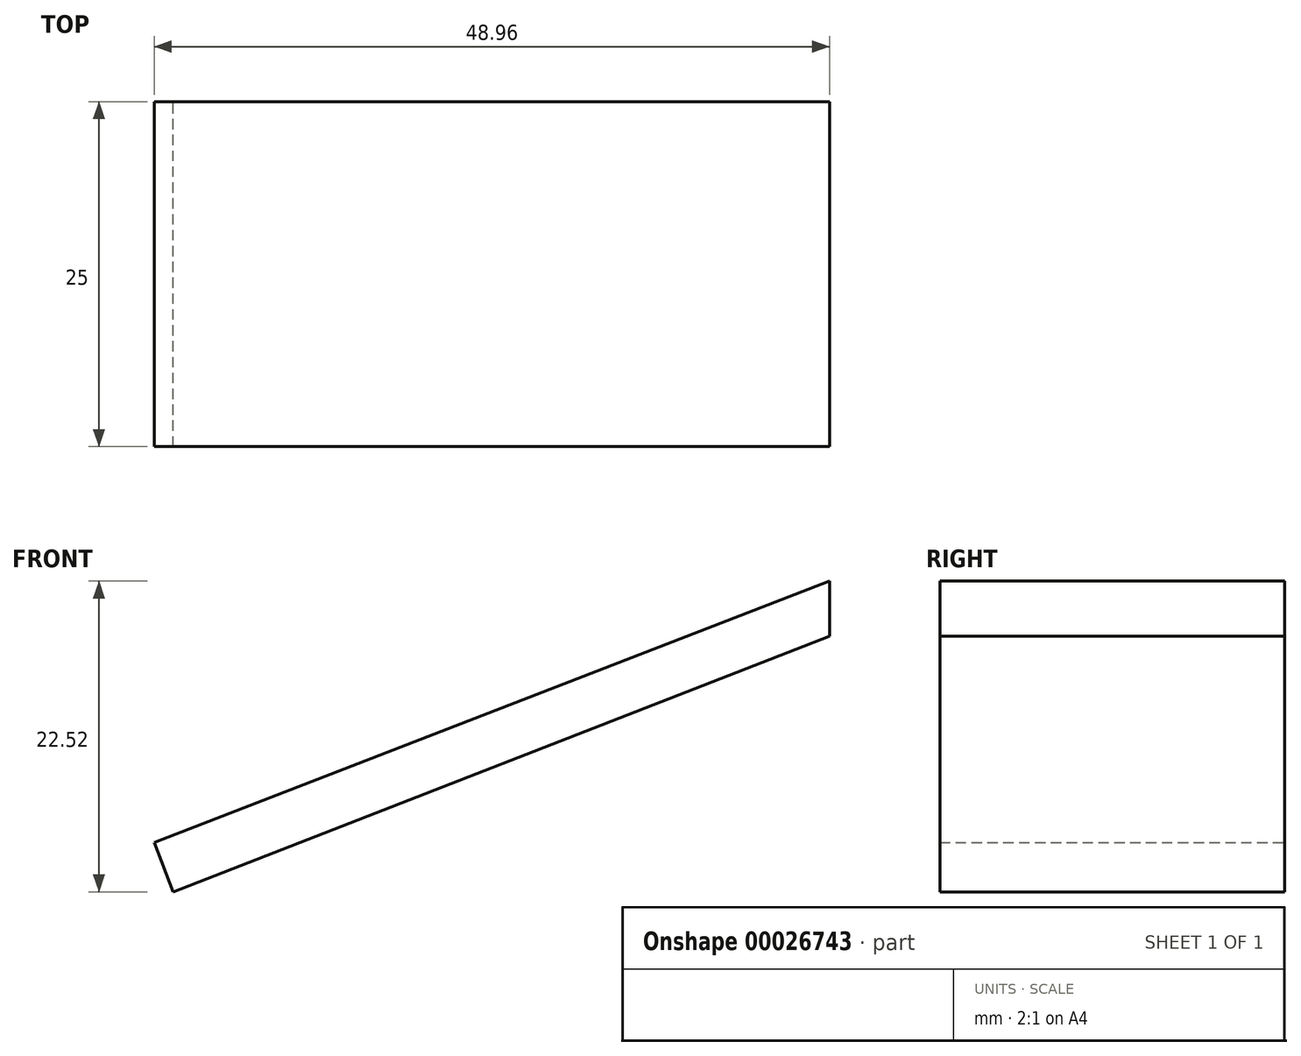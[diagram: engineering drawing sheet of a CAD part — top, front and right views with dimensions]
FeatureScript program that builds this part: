
annotation { "Feature Type Name" : "Feature", "Feature Type Description" : "" }
export const myFeature = defineFeature(function(context is Context, id is Id, definition is map)
    precondition{}
    {
        {
            var Q0;
            Q0=qCreatedBy(makeId("Front.planeOp"),FACE);
            var sketch = newSketch(context, id + "F0", { "sketchPlane" : qUnion([Q0])});
            skLineSegment(sketch, "E0", {"start": v(3.9, 17.02) * mm, "end": v(3.9, 13.02) * mm});
            skLineSegment(sketch, "E1", {"start": v(3.9, 13.02) * mm, "end": v(-43.68, -5.5) * mm});
            skLineSegment(sketch, "E2", {"start": v(-43.68, -5.5) * mm, "end": v(-45.07, -1.92) * mm});
            skLineSegment(sketch, "E3", {"start": v(-45.07, -1.92) * mm, "end": v(3.9, 17.02) * mm});
            skSolve(sketch);
        }
        {
            var Q0;
            Q0 = qSketchRegion(id + "F0", true);
            extrude(context, id + "F1", {"entities" : qUnion([Q0]), "depth" : 25 * mm});
        }
    });
